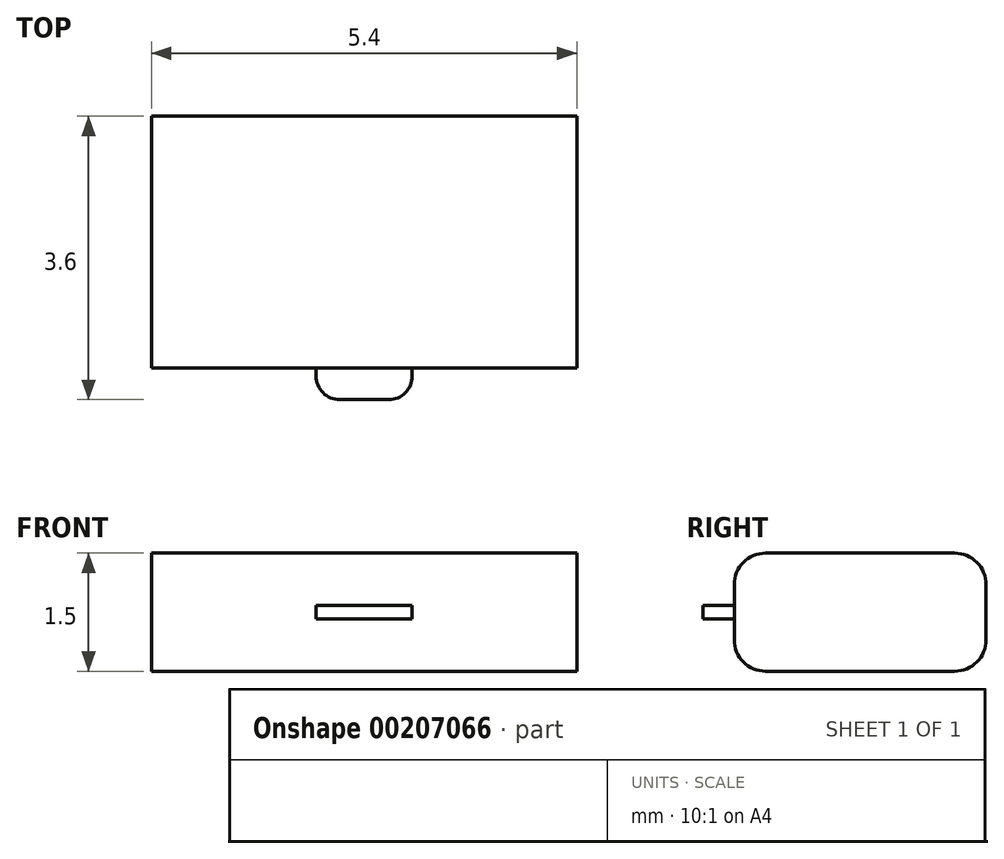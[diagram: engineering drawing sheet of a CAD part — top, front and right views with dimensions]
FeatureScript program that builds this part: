
annotation { "Feature Type Name" : "Feature", "Feature Type Description" : "" }
export const myFeature = defineFeature(function(context is Context, id is Id, definition is map)
    precondition{}
    {
        {
            var Q0;
            Q0=qCreatedBy(makeId("Top.planeOp"),FACE);
            var sketch = newSketch(context, id + "F0", { "sketchPlane" : qUnion([Q0])});
            skLineSegment(sketch, "E0.bottom", {"start": v(2.7, -1.6) * mm, "end": v(-2.7, -1.6) * mm});
            skLineSegment(sketch, "E0.top", {"start": v(2.7, 1.6) * mm, "end": v(-2.7, 1.6) * mm});
            skLineSegment(sketch, "E0.left", {"start": v(2.7, -1.6) * mm, "end": v(2.7, 1.6) * mm});
            skLineSegment(sketch, "E0.right", {"start": v(-2.7, -1.6) * mm, "end": v(-2.7, 1.6) * mm});
            skPoint(sketch, "E0.middle", {"position": v(0, 0) * mm});
            skSolve(sketch);
        }
        {
            var Q0;
            Q0=makeQuery(id+"F0.imprint","IMPRINT",FACE,{"disambiguationData":[TD([[makeQuery(id+"F0.imprint","IMPRINT",EDGE,{"derivedFrom":sQuery(id+"F0.wireOp",EDGE,"E0.bottom")}),-1.0]])]});
            extrude(context, id + "F1", {"entities" : qUnion([Q0]), "depth" : 1.5 * mm});
        }
        {
            var Q0;
            Q0=makeQuery(id+"F1.opExtrude","CAP_EDGE",EDGE,{"disambiguationData":[OSD([sQuery(id+"F0.wireOp",EDGE,"E0.bottom")])],"isStart":false});
            var Q1;
            Q1=makeQuery(id+"F1.opExtrude","CAP_EDGE",EDGE,{"disambiguationData":[OSD([sQuery(id+"F0.wireOp",EDGE,"E0.bottom")])],"isStart":true});
            var Q2;
            Q2=makeQuery(id+"F1.opExtrude","CAP_EDGE",EDGE,{"disambiguationData":[OSD([sQuery(id+"F0.wireOp",EDGE,"E0.top")])],"isStart":false});
            var Q3;
            Q3=makeQuery(id+"F1.opExtrude","CAP_EDGE",EDGE,{"disambiguationData":[OSD([sQuery(id+"F0.wireOp",EDGE,"E0.top")])],"isStart":true});
            fillet(context, id + "F2", {"entities" : qUnion([Q0, Q1, Q2, Q3]), "radius" : 0.4 * mm, "tangentPropagation" : true, "allowEdgeOverflow" : false});
        }
        {
            var Q0;
            Q0=makeQuery(id+"F1.opExtrude","SWEPT_FACE",FACE,{"disambiguationData":[OSD([sQuery(id+"F0.wireOp",EDGE,"E0.bottom")])]});
            var sketch = newSketch(context, id + "F3", { "sketchPlane" : qUnion([Q0])});
            skLineSegment(sketch, "E1.bottom", {"start": v(0.61, 0.66) * mm, "end": v(-0.61, 0.66) * mm});
            skLineSegment(sketch, "E1.top", {"start": v(0.61, 0.84) * mm, "end": v(-0.61, 0.84) * mm});
            skLineSegment(sketch, "E1.left", {"start": v(0.61, 0.66) * mm, "end": v(0.61, 0.84) * mm});
            skLineSegment(sketch, "E1.right", {"start": v(-0.61, 0.66) * mm, "end": v(-0.61, 0.84) * mm});
            skPoint(sketch, "E1.middle", {"position": v(0, 0.75) * mm});
            skPoint(sketch, "E1.middle.positionSnap0", {"position": v(-2.7, 0.75) * mm});
            skPoint(sketch, "E1.middle.positionSnap1", {"position": v(0, 1.1) * mm});
            skPoint(sketch, "E1.centerSnap0", {"position": v(-2.7, 0.75) * mm});
            skPoint(sketch, "E1.centerSnap1", {"position": v(0, 1.1) * mm});
            skSolve(sketch);
        }
        {
            var Q0;
            Q0=makeQuery(id+"F3.imprint","IMPRINT",FACE,{"disambiguationData":[TD([[makeQuery(id+"F3.imprint","IMPRINT",EDGE,{"derivedFrom":sQuery(id+"F3.wireOp",EDGE,"E1.bottom")}),-1.0]])]});
            extrude(context, id + "F4", {"entities" : qUnion([Q0]), "operationType" : NewBodyOperationType.ADD, "depth" : 0.4 * mm});
        }
        {
            var Q0;
            Q0=makeQuery(id+"F4.opExtrude","CAP_EDGE",EDGE,{"disambiguationData":[OSD([sQuery(id+"F3.wireOp",EDGE,"E1.right")])],"isStart":false});
            var Q1;
            Q1=makeQuery(id+"F4.opExtrude","CAP_EDGE",EDGE,{"disambiguationData":[OSD([sQuery(id+"F3.wireOp",EDGE,"E1.left")])],"isStart":false});
            fillet(context, id + "F5", {"entities" : qUnion([Q0, Q1]), "radius" : 0.3 * mm, "tangentPropagation" : true, "allowEdgeOverflow" : false});
        }
    });
